# Revit family: 318_26000f9ed1554a22b1ba4c8fe3c83b
name_source: partatom
category: Pipe Accessories
units: mm (PartAtom-declared; Revit-internal decimal feet)

## family parameters
Always vertical = Yes
Cut with Voids When Loaded = No
Part Type = Valve - Normal
Round Connector Dimension = Use Diameter
Shared = No
Work Plane-Based = No

## types (1)
- 2192 11403
    B = 1005 mm  [stored 3.29724 ft]
    BB = 144 mm
    BLL = 101 mm
    C = 65 mm  [stored 0.213255 ft]
    CenSd_DM2_6 = 14 mm  [stored 0.0459318 ft]
    CenSd_DM3_6 = 17 mm
    CenSd_RT1_6 = 14 mm  [stored 0.0459318 ft]
    CenSd_RT2_6 = 10 mm  [stored 0.0328084 ft]
    D = 25 mm
    DM2 = 16 mm
    DM3 = 20 mm  [stored 0.0656168 ft]
    Description = Central heating distr. unit, 3+1 ports, 1"1/4 side conn.
    E12 = 33 mm  [stored 0.108268 ft]
    E12__ve = -33 mm  [stored -0.108268 ft]
    E2 = 48 mm  [stored 0.15748 ft]
    E3 = 19 mm
    E4 = 10 mm  [stored 0.0328084 ft]
    EE = 8 mm  [stored 0.0262467 ft]
    ER = 5 mm  [stored 0.0164042 ft]
    F = 125 mm  [stored 0.410105 ft]
    FT = 15 mm  [stored 0.0492126 ft]
    FT__ve = -15 mm  [stored -0.0492126 ft]
    G2 = 130 mm  [stored 0.426509 ft]
    G2__ve = -130 mm  [stored -0.426509 ft]
    H = 125 mm  [stored 0.410105 ft]
    HH = 83 mm  [stored 0.27231 ft]
    HH__ve = -83 mm  [stored -0.27231 ft]
    HT1 = 102 mm  [stored 0.334646 ft]
    L = 200 mm  [stored 0.656168 ft]
    L1 = 15 mm  [stored 0.0492126 ft]
    L1__ve = -15 mm  [stored -0.0492126 ft]
    LL = 100 mm  [stored 0.328084 ft]
    LM = 140 mm  [stored 0.459318 ft]
    MC Product Code = 2192 11403
    MP1 = 32 mm
    MP3 = 32 mm
    Manufacturer = FAR
    N3 = Yes
    NR = 7 mm  [stored 0.0229659 ft]
    NR1 = 9 mm  [stored 0.0295276 ft]
    QmdConnectorList = 321;MP1;322;D;323;D;324;D;351;MP3;352;D;353;D;354;D
    R = 13 mm  [stored 0.0426509 ft]
    R2 = 8 mm  [stored 0.0262467 ft]
    RR = 13 mm  [stored 0.0426509 ft]
    RR3 = 15 mm  [stored 0.0492126 ft]
    RT = 8 mm  [stored 0.0262467 ft]
    RT1 = 16 mm
    RT2 = 12 mm  [stored 0.0393701 ft]
    TR = 23 mm
    TR1 = 29 mm
    magiPartTypeId = 318
    magiProductFamilyId = 26000f9ed1554a22b1ba4c8fe3c83b
    magiProductId = 26000f9ed1554a22b1ba4c8fe3c83b

note: [stored X ft] marks values corroborated as IEEE doubles in the binary element streams (Revit-internal decimal feet)

## geometry (parser evidence)
native form markers: Sweep x3
no freeform markers — native parametric forms only
